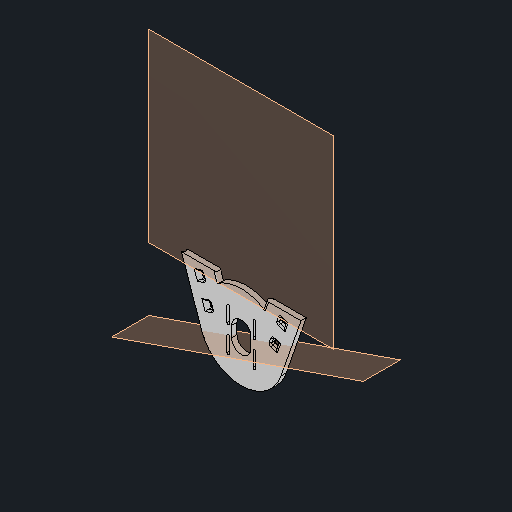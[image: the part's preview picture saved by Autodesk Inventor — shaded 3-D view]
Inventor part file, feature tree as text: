
AUTODESK INVENTOR PART (.ipt)
format: ipt  version: 2024 (Build 280153000, 153)  size: 356,864 bytes
history: native  units: in
note: dims shown in document units (in); Inventor stores cm internally (conversion verified against a paired STEP export)
features: reference x39, other x3, plane x2, extrude x2, fillet x2, sketch x2
ambient origin geometry x8: Origin, YZ Plane, XZ Plane, XY Plane, X Axis, Y Axis, Z Axis, Center Point
bodies: Solid1 (feature_tree)
feature tree (50):
  plane  "Work Plane1"
  extrude  "Extrusion1"  Depth=0.125in
  fillet  "Fillet1"  [1 undecoded]
  plane  "Work Plane2"
  extrude  "Extrusion2"  Depth=0.0625in
  fillet  "Fillet2"  [1 undecoded]
  sketch  "Sketch1"  dims[d0=0.25in d1=0.0in d2=0.125in d3=0.0in d4=0.0in]
  reference  "Reference1"
  reference  "Reference2"
  reference  "Reference3"
  reference  "Reference4"
  reference  "Reference5"
  reference  "Reference6"
  reference  "Reference7"
  reference  "Reference8"
  reference  "Reference9"
  reference  "Reference10"
  reference  "Reference11"
  reference  "Reference12"
  reference  "Reference13"
  reference  "Reference14"
  reference  "Reference15"
  reference  "Reference16"
  reference  "Reference17"
  reference  "Reference18"
  reference  "Reference19"
  reference  "Reference20"
  reference  "Reference21"
  reference  "Reference22"
  reference  "Reference23"
  reference  "Reference24"
  reference  "Reference25"
  reference  "Reference26"
  reference  "Reference27"
  reference  "Reference28"
  reference  "Reference29"
  reference  "Reference30"
  reference  "Reference31"
  reference  "Reference32"
  reference  "Reference33"
  reference  "Reference34"
  reference  "Reference35"
  reference  "Reference36"
  reference  "Reference37"
  sketch  "Sketch2"  dims[d5=0.125in d6=0.0625in]
  reference  "Reference38"
  reference  "Reference39"
  other  "<userpath>\CodingProjects\C-AAM\CAD\V1\BoardAssembly.iam"
  other  "BoardAssembly.iam"
  other  "Board:1"
note: 2 required parameter values undecoded (feature->parameter linkage not recoverable at this tier; creation-order binding heuristic only, values carry confidence <= 0.55)
